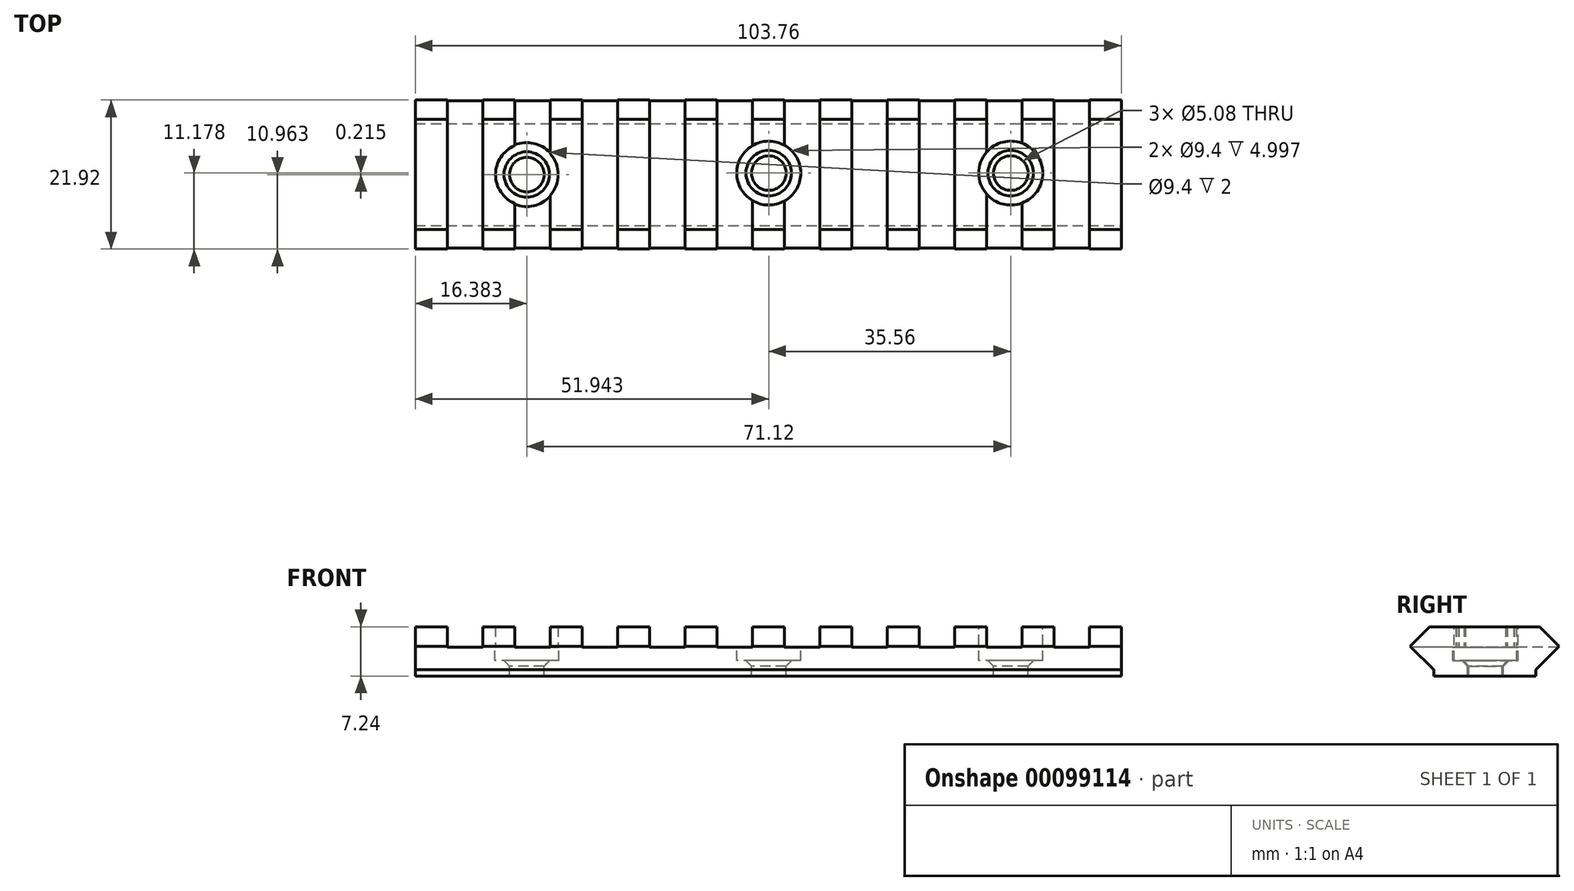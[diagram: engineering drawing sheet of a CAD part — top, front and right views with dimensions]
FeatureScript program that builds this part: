
annotation { "Feature Type Name" : "Feature", "Feature Type Description" : "" }
export const myFeature = defineFeature(function(context is Context, id is Id, definition is map)
    precondition{}
    {
        {
            var Q0;
            Q0=qCreatedBy(makeId("Right.planeOp"),FACE);
            var sketch = newSketch(context, id + "F0", { "sketchPlane" : qUnion([Q0])});
            skLineSegment(sketch, "E0", {"start": v(0, 0) * mm, "end": v(0, 1.52) * mm});
            skLineSegment(sketch, "E1", {"start": v(0, 1.52) * mm, "end": v(-2.86, 4.38) * mm});
            skLineSegment(sketch, "E2", {"start": v(-2.86, 4.38) * mm, "end": v(0, 7.24) * mm});
            skLineSegment(sketch, "E3", {"start": v(0, 7.24) * mm, "end": v(16.2, 7.24) * mm});
            skLineSegment(sketch, "E4", {"start": v(0, 0) * mm, "end": v(16.2, 0) * mm});
            skLineSegment(sketch, "E5", {"start": v(16.2, 0) * mm, "end": v(16.2, 1.52) * mm});
            skLineSegment(sketch, "E6", {"start": v(16.2, 1.52) * mm, "end": v(19.06, 4.38) * mm});
            skLineSegment(sketch, "E7", {"start": v(19.06, 4.38) * mm, "end": v(16.2, 7.24) * mm});
            skSolve(sketch);
        }
        {
            var Q0;
            Q0=makeQuery(id+"F0.imprint","IMPRINT",FACE,{"disambiguationData":[TD([[makeQuery(id+"F0.imprint","IMPRINT",EDGE,{"derivedFrom":sQuery(id+"F0.wireOp",EDGE,"E0")}),-1.0]])]});
            extrude(context, id + "F1", {"entities" : qUnion([Q0]), "depth" : 103.76 * mm});
        }
        {
            var Q0;
            Q0=makeQuery(id+"F1.opExtrude","SWEPT_FACE",FACE,{"disambiguationData":[OSD([sQuery(id+"F0.wireOp",EDGE,"E3")])]});
            var sketch = newSketch(context, id + "F2", { "sketchPlane" : qUnion([Q0])});
            skLineSegment(sketch, "E8", {"start": v(0, 8.1) * mm, "end": v(4.7, 8.1) * mm, "construction": true});
            skLineSegment(sketch, "E9", {"start": v(4.7, 8.1) * mm, "end": v(4.7, 19.06) * mm});
            skLineSegment(sketch, "E10", {"start": v(4.7, 8.1) * mm, "end": v(4.7, -2.86) * mm});
            skLineSegment(sketch, "E11", {"start": v(4.7, 8.1) * mm, "end": v(9.9, 8.1) * mm, "construction": true});
            skLineSegment(sketch, "E12", {"start": v(4.7, 19.06) * mm, "end": v(9.9, 19.06) * mm});
            skLineSegment(sketch, "E13", {"start": v(9.9, 19.06) * mm, "end": v(9.9, -2.86) * mm});
            skLineSegment(sketch, "E14", {"start": v(4.7, -2.86) * mm, "end": v(9.9, -2.86) * mm});
            skLineSegment(sketch, "E15", {"start": v(9.9, 8.1) * mm, "end": v(14.6, 8.1) * mm, "construction": true});
            skLineSegment(sketch, "E16.bottom", {"start": v(14.6, 19.06) * mm, "end": v(19.81, 19.06) * mm});
            skLineSegment(sketch, "E16.top", {"start": v(14.6, -2.86) * mm, "end": v(19.81, -2.86) * mm});
            skLineSegment(sketch, "E16.left", {"start": v(14.6, 19.06) * mm, "end": v(14.6, -2.86) * mm});
            skLineSegment(sketch, "E16.right", {"start": v(19.81, 19.06) * mm, "end": v(19.81, -2.86) * mm});
            skLineSegment(sketch, "E17", {"start": v(19.81, 8.1) * mm, "end": v(24.51, 8.1) * mm, "construction": true});
            skLineSegment(sketch, "E18.bottom", {"start": v(24.51, 19.06) * mm, "end": v(29.72, 19.06) * mm});
            skLineSegment(sketch, "E18.top", {"start": v(24.51, -2.86) * mm, "end": v(29.72, -2.86) * mm});
            skLineSegment(sketch, "E18.left", {"start": v(24.51, 19.06) * mm, "end": v(24.51, -2.86) * mm});
            skLineSegment(sketch, "E18.right", {"start": v(29.72, 19.06) * mm, "end": v(29.72, -2.86) * mm});
            skLineSegment(sketch, "E19.bottom", {"start": v(34.42, 19.06) * mm, "end": v(39.62, 19.06) * mm});
            skLineSegment(sketch, "E19.top", {"start": v(34.42, -2.86) * mm, "end": v(39.62, -2.86) * mm});
            skLineSegment(sketch, "E19.left", {"start": v(34.42, 19.06) * mm, "end": v(34.42, -2.86) * mm});
            skLineSegment(sketch, "E19.right", {"start": v(39.62, 19.06) * mm, "end": v(39.62, -2.86) * mm});
            skLineSegment(sketch, "E20", {"start": v(39.62, 8.1) * mm, "end": v(44.32, 8.1) * mm, "construction": true});
            skLineSegment(sketch, "E21.bottom", {"start": v(44.32, 19.06) * mm, "end": v(49.53, 19.06) * mm});
            skLineSegment(sketch, "E21.top", {"start": v(44.32, -2.86) * mm, "end": v(49.53, -2.86) * mm});
            skLineSegment(sketch, "E21.left", {"start": v(44.32, 19.06) * mm, "end": v(44.32, -2.86) * mm});
            skLineSegment(sketch, "E21.right", {"start": v(49.53, 19.06) * mm, "end": v(49.53, -2.86) * mm});
            skLineSegment(sketch, "E22", {"start": v(49.53, 8.1) * mm, "end": v(54.23, 8.1) * mm, "construction": true});
            skLineSegment(sketch, "E23.bottom", {"start": v(54.23, 19.06) * mm, "end": v(59.44, 19.06) * mm});
            skLineSegment(sketch, "E23.top", {"start": v(54.23, -2.86) * mm, "end": v(59.44, -2.86) * mm});
            skLineSegment(sketch, "E23.left", {"start": v(54.23, 19.06) * mm, "end": v(54.23, -2.86) * mm});
            skLineSegment(sketch, "E23.right", {"start": v(59.44, 19.06) * mm, "end": v(59.44, -2.86) * mm});
            skLineSegment(sketch, "E24", {"start": v(59.44, 8.1) * mm, "end": v(64.13, 8.1) * mm, "construction": true});
            skLineSegment(sketch, "E25.bottom", {"start": v(64.13, 19.06) * mm, "end": v(69.34, 19.06) * mm});
            skLineSegment(sketch, "E25.top", {"start": v(64.13, -2.86) * mm, "end": v(69.34, -2.86) * mm});
            skLineSegment(sketch, "E25.left", {"start": v(64.13, 19.06) * mm, "end": v(64.13, -2.86) * mm});
            skLineSegment(sketch, "E25.right", {"start": v(69.34, 19.06) * mm, "end": v(69.34, -2.86) * mm});
            skLineSegment(sketch, "E26", {"start": v(69.34, 8.1) * mm, "end": v(74.04, 8.1) * mm, "construction": true});
            skLineSegment(sketch, "E27", {"start": v(29.72, 8.1) * mm, "end": v(34.42, 8.1) * mm, "construction": true});
            skLineSegment(sketch, "E28.bottom", {"start": v(74.04, 19.06) * mm, "end": v(79.25, 19.06) * mm});
            skLineSegment(sketch, "E28.top", {"start": v(74.04, -2.86) * mm, "end": v(79.25, -2.86) * mm});
            skLineSegment(sketch, "E28.left", {"start": v(74.04, 19.06) * mm, "end": v(74.04, -2.86) * mm});
            skLineSegment(sketch, "E28.right", {"start": v(79.25, 19.06) * mm, "end": v(79.25, -2.86) * mm});
            skLineSegment(sketch, "E29", {"start": v(79.25, 8.1) * mm, "end": v(83.95, 8.1) * mm, "construction": true});
            skLineSegment(sketch, "E30.bottom", {"start": v(83.95, 19.06) * mm, "end": v(89.15, 19.06) * mm});
            skLineSegment(sketch, "E30.top", {"start": v(83.95, -2.86) * mm, "end": v(89.15, -2.86) * mm});
            skLineSegment(sketch, "E30.left", {"start": v(83.95, 19.06) * mm, "end": v(83.95, -2.86) * mm});
            skLineSegment(sketch, "E30.right", {"start": v(89.15, 19.06) * mm, "end": v(89.15, -2.86) * mm});
            skLineSegment(sketch, "E31", {"start": v(89.15, 8.1) * mm, "end": v(93.85, 8.1) * mm, "construction": true});
            skLineSegment(sketch, "E32.bottom", {"start": v(93.85, 19.15) * mm, "end": v(99.06, 19.15) * mm});
            skLineSegment(sketch, "E32.top", {"start": v(93.85, -2.94) * mm, "end": v(99.06, -2.94) * mm});
            skLineSegment(sketch, "E32.left", {"start": v(93.85, 19.15) * mm, "end": v(93.85, -2.94) * mm});
            skLineSegment(sketch, "E32.right", {"start": v(99.06, 19.15) * mm, "end": v(99.06, -2.94) * mm});
            skSolve(sketch);
        }
        {
            var Q0;
            {var subQ0=sQuery(id+"F2.wireOp",EDGE,"E14");Q0=makeQuery(id+"F2.imprint","IMPRINT",FACE,{"disambiguationData":[TD([[makeQuery(id+"F2.imprint","IMPRINT",EDGE,{"derivedFrom":subQ0}),1.0]])]});}
            var Q1;
            {var subQ0=sQuery(id+"F2.wireOp",EDGE,"E10");var subQ8=sQuery(id+"F2.wireOp",EDGE,"E9");var subQ9=makeQuery(id+"F2.imprint","INTERSECT",VERTEX,{"derivedFrom":[subQ8,subQ0]});Q1=makeQuery(id+"F2.imprint","IMPRINT",FACE,{"disambiguationData":[TD([[makeQuery(id+"F2.imprint","IMPRINT",EDGE,{"disambiguationData":[TD([[subQ9,-1.0]])],"derivedFrom":subQ8}),-1.0]])]});}
            var Q2;
            {var subQ0=sQuery(id+"F2.wireOp",EDGE,"E12");Q2=makeQuery(id+"F2.imprint","IMPRINT",FACE,{"disambiguationData":[TD([[makeQuery(id+"F2.imprint","IMPRINT",EDGE,{"derivedFrom":subQ0}),-1.0]])]});}
            var Q3;
            {var subQ0=sQuery(id+"F2.wireOp",EDGE,"E16.bottom");Q3=makeQuery(id+"F2.imprint","IMPRINT",FACE,{"disambiguationData":[TD([[makeQuery(id+"F2.imprint","IMPRINT",EDGE,{"derivedFrom":subQ0}),-1.0]])]});}
            var Q4;
            {var subQ0=sQuery(id+"F2.wireOp",EDGE,"E16.left");var subQ1=sQuery(id+"F0.wireOp",EDGE,"E3");var subQ2=makeQuery(id+"F1.opExtrude","SWEPT_EDGE",EDGE,{"disambiguationData":[OSD([subQ1,sQuery(id+"F0.wireOp",EDGE,"E7")])]});var subQ3=makeQuery(id+"F2.imprint","INTERSECT",VERTEX,{"derivedFrom":[subQ2,subQ0]});Q4=makeQuery(id+"F2.imprint","IMPRINT",FACE,{"disambiguationData":[TD([[makeQuery(id+"F2.imprint","IMPRINT",EDGE,{"disambiguationData":[TD([[subQ3,-1.0]])],"derivedFrom":subQ0}),1.0]])]});}
            var Q5;
            {var subQ0=sQuery(id+"F2.wireOp",EDGE,"E16.top");Q5=makeQuery(id+"F2.imprint","IMPRINT",FACE,{"disambiguationData":[TD([[makeQuery(id+"F2.imprint","IMPRINT",EDGE,{"derivedFrom":subQ0}),1.0]])]});}
            var Q6;
            {var subQ0=sQuery(id+"F2.wireOp",EDGE,"E18.bottom");Q6=makeQuery(id+"F2.imprint","IMPRINT",FACE,{"disambiguationData":[TD([[makeQuery(id+"F2.imprint","IMPRINT",EDGE,{"derivedFrom":subQ0}),-1.0]])]});}
            var Q7;
            {var subQ0=sQuery(id+"F2.wireOp",EDGE,"E18.left");var subQ1=sQuery(id+"F0.wireOp",EDGE,"E3");var subQ2=makeQuery(id+"F1.opExtrude","SWEPT_EDGE",EDGE,{"disambiguationData":[OSD([subQ1,sQuery(id+"F0.wireOp",EDGE,"E7")])]});var subQ3=makeQuery(id+"F2.imprint","INTERSECT",VERTEX,{"derivedFrom":[subQ2,subQ0]});Q7=makeQuery(id+"F2.imprint","IMPRINT",FACE,{"disambiguationData":[TD([[makeQuery(id+"F2.imprint","IMPRINT",EDGE,{"disambiguationData":[TD([[subQ3,-1.0]])],"derivedFrom":subQ0}),1.0]])]});}
            var Q8;
            {var subQ0=sQuery(id+"F2.wireOp",EDGE,"E18.top");Q8=makeQuery(id+"F2.imprint","IMPRINT",FACE,{"disambiguationData":[TD([[makeQuery(id+"F2.imprint","IMPRINT",EDGE,{"derivedFrom":subQ0}),1.0]])]});}
            var Q9;
            {var subQ0=sQuery(id+"F2.wireOp",EDGE,"E19.bottom");Q9=makeQuery(id+"F2.imprint","IMPRINT",FACE,{"disambiguationData":[TD([[makeQuery(id+"F2.imprint","IMPRINT",EDGE,{"derivedFrom":subQ0}),-1.0]])]});}
            var Q10;
            {var subQ0=sQuery(id+"F2.wireOp",EDGE,"E19.left");var subQ1=sQuery(id+"F0.wireOp",EDGE,"E3");var subQ2=makeQuery(id+"F1.opExtrude","SWEPT_EDGE",EDGE,{"disambiguationData":[OSD([subQ1,sQuery(id+"F0.wireOp",EDGE,"E7")])]});var subQ3=makeQuery(id+"F2.imprint","INTERSECT",VERTEX,{"derivedFrom":[subQ2,subQ0]});Q10=makeQuery(id+"F2.imprint","IMPRINT",FACE,{"disambiguationData":[TD([[makeQuery(id+"F2.imprint","IMPRINT",EDGE,{"disambiguationData":[TD([[subQ3,-1.0]])],"derivedFrom":subQ0}),1.0]])]});}
            var Q11;
            {var subQ0=sQuery(id+"F2.wireOp",EDGE,"E19.top");Q11=makeQuery(id+"F2.imprint","IMPRINT",FACE,{"disambiguationData":[TD([[makeQuery(id+"F2.imprint","IMPRINT",EDGE,{"derivedFrom":subQ0}),1.0]])]});}
            var Q12;
            {var subQ0=sQuery(id+"F2.wireOp",EDGE,"E21.bottom");Q12=makeQuery(id+"F2.imprint","IMPRINT",FACE,{"disambiguationData":[TD([[makeQuery(id+"F2.imprint","IMPRINT",EDGE,{"derivedFrom":subQ0}),-1.0]])]});}
            var Q13;
            {var subQ0=sQuery(id+"F2.wireOp",EDGE,"E21.left");var subQ1=sQuery(id+"F0.wireOp",EDGE,"E3");var subQ2=makeQuery(id+"F1.opExtrude","SWEPT_EDGE",EDGE,{"disambiguationData":[OSD([subQ1,sQuery(id+"F0.wireOp",EDGE,"E7")])]});var subQ3=makeQuery(id+"F2.imprint","INTERSECT",VERTEX,{"derivedFrom":[subQ2,subQ0]});Q13=makeQuery(id+"F2.imprint","IMPRINT",FACE,{"disambiguationData":[TD([[makeQuery(id+"F2.imprint","IMPRINT",EDGE,{"disambiguationData":[TD([[subQ3,-1.0]])],"derivedFrom":subQ0}),1.0]])]});}
            var Q14;
            {var subQ0=sQuery(id+"F2.wireOp",EDGE,"E21.top");Q14=makeQuery(id+"F2.imprint","IMPRINT",FACE,{"disambiguationData":[TD([[makeQuery(id+"F2.imprint","IMPRINT",EDGE,{"derivedFrom":subQ0}),1.0]])]});}
            var Q15;
            {var subQ0=sQuery(id+"F2.wireOp",EDGE,"E23.bottom");Q15=makeQuery(id+"F2.imprint","IMPRINT",FACE,{"disambiguationData":[TD([[makeQuery(id+"F2.imprint","IMPRINT",EDGE,{"derivedFrom":subQ0}),-1.0]])]});}
            var Q16;
            {var subQ0=sQuery(id+"F2.wireOp",EDGE,"E23.left");var subQ1=sQuery(id+"F0.wireOp",EDGE,"E3");var subQ2=makeQuery(id+"F1.opExtrude","SWEPT_EDGE",EDGE,{"disambiguationData":[OSD([subQ1,sQuery(id+"F0.wireOp",EDGE,"E7")])]});var subQ3=makeQuery(id+"F2.imprint","INTERSECT",VERTEX,{"derivedFrom":[subQ2,subQ0]});Q16=makeQuery(id+"F2.imprint","IMPRINT",FACE,{"disambiguationData":[TD([[makeQuery(id+"F2.imprint","IMPRINT",EDGE,{"disambiguationData":[TD([[subQ3,-1.0]])],"derivedFrom":subQ0}),1.0]])]});}
            var Q17;
            {var subQ0=sQuery(id+"F2.wireOp",EDGE,"E23.top");Q17=makeQuery(id+"F2.imprint","IMPRINT",FACE,{"disambiguationData":[TD([[makeQuery(id+"F2.imprint","IMPRINT",EDGE,{"derivedFrom":subQ0}),1.0]])]});}
            var Q18;
            {var subQ0=sQuery(id+"F2.wireOp",EDGE,"E25.bottom");Q18=makeQuery(id+"F2.imprint","IMPRINT",FACE,{"disambiguationData":[TD([[makeQuery(id+"F2.imprint","IMPRINT",EDGE,{"derivedFrom":subQ0}),-1.0]])]});}
            var Q19;
            {var subQ0=sQuery(id+"F2.wireOp",EDGE,"E25.left");var subQ1=sQuery(id+"F0.wireOp",EDGE,"E3");var subQ2=makeQuery(id+"F1.opExtrude","SWEPT_EDGE",EDGE,{"disambiguationData":[OSD([subQ1,sQuery(id+"F0.wireOp",EDGE,"E7")])]});var subQ3=makeQuery(id+"F2.imprint","INTERSECT",VERTEX,{"derivedFrom":[subQ2,subQ0]});Q19=makeQuery(id+"F2.imprint","IMPRINT",FACE,{"disambiguationData":[TD([[makeQuery(id+"F2.imprint","IMPRINT",EDGE,{"disambiguationData":[TD([[subQ3,-1.0]])],"derivedFrom":subQ0}),1.0]])]});}
            var Q20;
            {var subQ0=sQuery(id+"F2.wireOp",EDGE,"E25.top");Q20=makeQuery(id+"F2.imprint","IMPRINT",FACE,{"disambiguationData":[TD([[makeQuery(id+"F2.imprint","IMPRINT",EDGE,{"derivedFrom":subQ0}),1.0]])]});}
            var Q21;
            {var subQ0=sQuery(id+"F2.wireOp",EDGE,"E28.bottom");Q21=makeQuery(id+"F2.imprint","IMPRINT",FACE,{"disambiguationData":[TD([[makeQuery(id+"F2.imprint","IMPRINT",EDGE,{"derivedFrom":subQ0}),-1.0]])]});}
            var Q22;
            {var subQ0=sQuery(id+"F2.wireOp",EDGE,"E28.left");var subQ1=sQuery(id+"F0.wireOp",EDGE,"E3");var subQ2=makeQuery(id+"F1.opExtrude","SWEPT_EDGE",EDGE,{"disambiguationData":[OSD([subQ1,sQuery(id+"F0.wireOp",EDGE,"E7")])]});var subQ3=makeQuery(id+"F2.imprint","INTERSECT",VERTEX,{"derivedFrom":[subQ2,subQ0]});Q22=makeQuery(id+"F2.imprint","IMPRINT",FACE,{"disambiguationData":[TD([[makeQuery(id+"F2.imprint","IMPRINT",EDGE,{"disambiguationData":[TD([[subQ3,-1.0]])],"derivedFrom":subQ0}),1.0]])]});}
            var Q23;
            {var subQ0=sQuery(id+"F2.wireOp",EDGE,"E28.top");Q23=makeQuery(id+"F2.imprint","IMPRINT",FACE,{"disambiguationData":[TD([[makeQuery(id+"F2.imprint","IMPRINT",EDGE,{"derivedFrom":subQ0}),1.0]])]});}
            var Q24;
            {var subQ0=sQuery(id+"F2.wireOp",EDGE,"E30.top");Q24=makeQuery(id+"F2.imprint","IMPRINT",FACE,{"disambiguationData":[TD([[makeQuery(id+"F2.imprint","IMPRINT",EDGE,{"derivedFrom":subQ0}),1.0]])]});}
            var Q25;
            {var subQ0=sQuery(id+"F2.wireOp",EDGE,"E30.left");var subQ1=sQuery(id+"F0.wireOp",EDGE,"E3");var subQ2=makeQuery(id+"F1.opExtrude","SWEPT_EDGE",EDGE,{"disambiguationData":[OSD([subQ1,sQuery(id+"F0.wireOp",EDGE,"E7")])]});var subQ3=makeQuery(id+"F2.imprint","INTERSECT",VERTEX,{"derivedFrom":[subQ2,subQ0]});Q25=makeQuery(id+"F2.imprint","IMPRINT",FACE,{"disambiguationData":[TD([[makeQuery(id+"F2.imprint","IMPRINT",EDGE,{"disambiguationData":[TD([[subQ3,-1.0]])],"derivedFrom":subQ0}),1.0]])]});}
            var Q26;
            {var subQ0=sQuery(id+"F2.wireOp",EDGE,"E30.bottom");Q26=makeQuery(id+"F2.imprint","IMPRINT",FACE,{"disambiguationData":[TD([[makeQuery(id+"F2.imprint","IMPRINT",EDGE,{"derivedFrom":subQ0}),-1.0]])]});}
            var Q27;
            {var subQ0=sQuery(id+"F2.wireOp",EDGE,"E32.bottom");Q27=makeQuery(id+"F2.imprint","IMPRINT",FACE,{"disambiguationData":[TD([[makeQuery(id+"F2.imprint","IMPRINT",EDGE,{"derivedFrom":subQ0}),-1.0]])]});}
            var Q28;
            {var subQ0=sQuery(id+"F2.wireOp",EDGE,"E32.left");var subQ1=sQuery(id+"F0.wireOp",EDGE,"E3");var subQ2=makeQuery(id+"F1.opExtrude","SWEPT_EDGE",EDGE,{"disambiguationData":[OSD([subQ1,sQuery(id+"F0.wireOp",EDGE,"E7")])]});var subQ3=makeQuery(id+"F2.imprint","INTERSECT",VERTEX,{"derivedFrom":[subQ2,subQ0]});Q28=makeQuery(id+"F2.imprint","IMPRINT",FACE,{"disambiguationData":[TD([[makeQuery(id+"F2.imprint","IMPRINT",EDGE,{"disambiguationData":[TD([[subQ3,-1.0]])],"derivedFrom":subQ0}),1.0]])]});}
            var Q29;
            {var subQ0=sQuery(id+"F2.wireOp",EDGE,"E32.top");Q29=makeQuery(id+"F2.imprint","IMPRINT",FACE,{"disambiguationData":[TD([[makeQuery(id+"F2.imprint","IMPRINT",EDGE,{"derivedFrom":subQ0}),1.0]])]});}
            extrude(context, id + "F3", {"entities" : qUnion([Q0, Q1, Q2, Q3, Q4, Q5, Q6, Q7, Q8, Q9, Q10, Q11, Q12, Q13, Q14, Q15, Q16, Q17, Q18, Q19, Q20, Q21, Q22, Q23, Q24, Q25, Q26, Q27, Q28, Q29]), "operationType" : NewBodyOperationType.REMOVE, "oppositeDirection" : true, "depth" : 3 * mm});
        }
        {
            var Q0;
            Q0=makeQuery(id+"F1.opExtrude","SWEPT_FACE",FACE,{"disambiguationData":[OSD([sQuery(id+"F0.wireOp",EDGE,"E4")])]});
            var sketch = newSketch(context, id + "F4", { "sketchPlane" : qUnion([Q0])});
            skCircle(sketch, "E33", {"center": v(87.5, -8.32) * mm, "radius": 2.54 * mm});
            skCircle(sketch, "E34", {"center": v(16.38, -8.1) * mm, "radius": 2.54 * mm});
            skLineSegment(sketch, "E35", {"start": v(16.38, -8.1) * mm, "end": v(0, -8.1) * mm, "construction": true});
            skPoint(sketch, "E35.endSnap0", {"position": v(0, -8.1) * mm});
            skCircle(sketch, "E36", {"center": v(51.94, -8.32) * mm, "radius": 2.54 * mm});
            skSolve(sketch);
        }
        {
            var Q0;
            Q0 = qSketchRegion(id + "F4", true);
            extrude(context, id + "F5", {"entities" : qUnion([Q0]), "operationType" : NewBodyOperationType.REMOVE, "endBound" : BoundingType.SYMMETRIC, "depth" : 25.4 * mm, "offsetDistance" : 25.4 * mm});
        }
        {
            var Q0;
            Q0=makeQuery(id+"F3.boolean.opBoolean","COPY",FACE,{"derivedFrom":makeQuery(id+"F3.opExtrude","CAP_FACE",FACE,{"disambiguationData":[OSD([sQuery(id+"F2.wireOp",EDGE,"E16.bottom"),sQuery(id+"F2.wireOp",EDGE,"E16.top"),sQuery(id+"F2.wireOp",EDGE,"E16.left"),sQuery(id+"F2.wireOp",EDGE,"E16.right")])],"isStart":false})});
            var sketch = newSketch(context, id + "F6", { "sketchPlane" : qUnion([Q0])});
            skCircle(sketch, "E37", {"center": v(16.38, 8.1) * mm, "radius": 4.6 * mm});
            skSolve(sketch);
        }
        {
            var Q0;
            Q0 = qSketchRegion(id + "F6", true);
            extrude(context, id + "F7", {"entities" : qUnion([Q0]), "operationType" : NewBodyOperationType.REMOVE, "depth" : 25.4 * mm, "offsetDistance" : 25.4 * mm});
        }
        {
            var Q0;
            Q0=makeQuery(id+"F3.boolean.opBoolean","COPY",FACE,{"derivedFrom":makeQuery(id+"F3.opExtrude","CAP_FACE",FACE,{"disambiguationData":[OSD([sQuery(id+"F2.wireOp",EDGE,"E30.bottom"),sQuery(id+"F2.wireOp",EDGE,"E30.top"),sQuery(id+"F2.wireOp",EDGE,"E30.left"),sQuery(id+"F2.wireOp",EDGE,"E30.right")])],"isStart":false})});
            var sketch = newSketch(context, id + "F8", { "sketchPlane" : qUnion([Q0])});
            skCircle(sketch, "E38", {"center": v(87.5, 8.32) * mm, "radius": 4.6 * mm});
            skSolve(sketch);
        }
        {
            var Q0;
            Q0 = qSketchRegion(id + "F8", true);
            extrude(context, id + "F9", {"entities" : qUnion([Q0]), "operationType" : NewBodyOperationType.REMOVE, "depth" : 25.4 * mm, "offsetDistance" : 25.4 * mm});
        }
        {
            var Q0;
            Q0=makeQuery(id+"F3.boolean.opBoolean","COPY",FACE,{"derivedFrom":makeQuery(id+"F3.opExtrude","CAP_FACE",FACE,{"disambiguationData":[OSD([sQuery(id+"F2.wireOp",EDGE,"E23.bottom"),sQuery(id+"F2.wireOp",EDGE,"E23.top"),sQuery(id+"F2.wireOp",EDGE,"E23.left"),sQuery(id+"F2.wireOp",EDGE,"E23.right")])],"isStart":false})});
            var sketch = newSketch(context, id + "F10", { "sketchPlane" : qUnion([Q0])});
            skCircle(sketch, "E39", {"center": v(51.94, 8.32) * mm, "radius": 4.6 * mm});
            skSolve(sketch);
        }
        {
            var Q0;
            Q0 = qSketchRegion(id + "F10", true);
            extrude(context, id + "F11", {"entities" : qUnion([Q0]), "operationType" : NewBodyOperationType.REMOVE, "depth" : 25.4 * mm, "offsetDistance" : 25.4 * mm});
        }
        {
            var Q0;
            Q0=makeQuery(id+"F1.opExtrude","CAP_FACE",FACE,{"disambiguationData":[OSD([sQuery(id+"F0.wireOp",EDGE,"E0"),sQuery(id+"F0.wireOp",EDGE,"E1"),sQuery(id+"F0.wireOp",EDGE,"E2"),sQuery(id+"F0.wireOp",EDGE,"E3"),sQuery(id+"F0.wireOp",EDGE,"E4"),sQuery(id+"F0.wireOp",EDGE,"E5"),sQuery(id+"F0.wireOp",EDGE,"E6"),sQuery(id+"F0.wireOp",EDGE,"E7")])],"isStart":false});
            var sketch = newSketch(context, id + "F12", { "sketchPlane" : qUnion([Q0])});
            skLineSegment(sketch, "E40", {"start": v(-2.86, 4.38) * mm, "end": v(0.6, 0.92) * mm});
            skLineSegment(sketch, "E41", {"start": v(19.06, 4.38) * mm, "end": v(15.6, 0.92) * mm});
            skLineSegment(sketch, "E42", {"start": v(0.6, 0) * mm, "end": v(0.6, 0.92) * mm});
            skLineSegment(sketch, "E43", {"start": v(-2.86, 4.38) * mm, "end": v(-2.86, 0) * mm});
            skLineSegment(sketch, "E44", {"start": v(-2.86, 0) * mm, "end": v(0.6, 0) * mm});
            skLineSegment(sketch, "E45", {"start": v(15.6, 0.92) * mm, "end": v(15.6, 0) * mm});
            skLineSegment(sketch, "E46", {"start": v(15.6, 0) * mm, "end": v(19.06, 0) * mm});
            skLineSegment(sketch, "E47", {"start": v(19.06, 0) * mm, "end": v(19.06, 4.38) * mm});
            skSolve(sketch);
        }
        {
            var Q0;
            Q0 = qSketchRegion(id + "F12", true);
            extrude(context, id + "F13", {"entities" : qUnion([Q0]), "operationType" : NewBodyOperationType.REMOVE, "oppositeDirection" : true, "depth" : 127 * mm, "offsetDistance" : 25.4 * mm});
        }
        {
            var Q0;
            Q0=makeQuery(id+"F7.boolean.opBoolean","MERGE",FACE,{"derivedFrom":[makeQuery(id+"F3.boolean.opBoolean","COPY",FACE,{"derivedFrom":makeQuery(id+"F3.opExtrude","CAP_FACE",FACE,{"disambiguationData":[OSD([sQuery(id+"F2.wireOp",EDGE,"E16.bottom"),sQuery(id+"F2.wireOp",EDGE,"E16.top"),sQuery(id+"F2.wireOp",EDGE,"E16.left"),sQuery(id+"F2.wireOp",EDGE,"E16.right")])],"isStart":false})})],"fromTools":[makeQuery(id+"F7.opExtrude","CAP_FACE",FACE,{"disambiguationData":[OSD([sQuery(id+"F6.wireOp",EDGE,"E37")])],"isStart":true})]});
            var sketch = newSketch(context, id + "F14", { "sketchPlane" : qUnion([Q0])});
            skCircle(sketch, "E48", {"center": v(16.38, 8.1) * mm, "radius": 4.7 * mm});
            skSolve(sketch);
        }
        {
            var Q0;
            Q0 = qSketchRegion(id + "F14", true);
            extrude(context, id + "F15", {"entities" : qUnion([Q0]), "operationType" : NewBodyOperationType.REMOVE, "oppositeDirection" : true, "depth" : 2 * mm, "offsetDistance" : 25.4 * mm});
        }
        {
            var Q0;
            Q0=makeQuery(id+"F11.boolean.opBoolean","MERGE",FACE,{"derivedFrom":[makeQuery(id+"F3.boolean.opBoolean","COPY",FACE,{"derivedFrom":makeQuery(id+"F3.opExtrude","CAP_FACE",FACE,{"disambiguationData":[OSD([sQuery(id+"F2.wireOp",EDGE,"E21.bottom"),sQuery(id+"F2.wireOp",EDGE,"E21.top"),sQuery(id+"F2.wireOp",EDGE,"E21.left"),sQuery(id+"F2.wireOp",EDGE,"E21.right")])],"isStart":false})}),makeQuery(id+"F3.boolean.opBoolean","COPY",FACE,{"derivedFrom":makeQuery(id+"F3.opExtrude","CAP_FACE",FACE,{"disambiguationData":[OSD([sQuery(id+"F2.wireOp",EDGE,"E23.bottom"),sQuery(id+"F2.wireOp",EDGE,"E23.top"),sQuery(id+"F2.wireOp",EDGE,"E23.left"),sQuery(id+"F2.wireOp",EDGE,"E23.right")])],"isStart":false})})],"fromTools":[makeQuery(id+"F11.opExtrude","CAP_FACE",FACE,{"disambiguationData":[OSD([sQuery(id+"F10.wireOp",EDGE,"E39")])],"isStart":true})]});
            var sketch = newSketch(context, id + "F16", { "sketchPlane" : qUnion([Q0])});
            skCircle(sketch, "E49", {"center": v(51.94, 8.32) * mm, "radius": 4.7 * mm});
            skSolve(sketch);
        }
        {
            var Q0;
            Q0 = qSketchRegion(id + "F16", true);
            extrude(context, id + "F17", {"entities" : qUnion([Q0]), "operationType" : NewBodyOperationType.REMOVE, "oppositeDirection" : true, "depth" : 2 * mm, "offsetDistance" : 25.4 * mm});
        }
        {
            var Q0;
            Q0 = qSketchRegion(id + "F16", true);
            extrude(context, id + "F18", {"entities" : qUnion([Q0]), "operationType" : NewBodyOperationType.REMOVE, "depth" : 25.4 * mm, "offsetDistance" : 25.4 * mm});
        }
        {
            var Q0;
            Q0=makeQuery(id+"F9.boolean.opBoolean","MERGE",FACE,{"derivedFrom":[makeQuery(id+"F3.boolean.opBoolean","COPY",FACE,{"derivedFrom":makeQuery(id+"F3.opExtrude","CAP_FACE",FACE,{"disambiguationData":[OSD([sQuery(id+"F2.wireOp",EDGE,"E30.bottom"),sQuery(id+"F2.wireOp",EDGE,"E30.top"),sQuery(id+"F2.wireOp",EDGE,"E30.left"),sQuery(id+"F2.wireOp",EDGE,"E30.right")])],"isStart":false})})],"fromTools":[makeQuery(id+"F9.opExtrude","CAP_FACE",FACE,{"disambiguationData":[OSD([sQuery(id+"F8.wireOp",EDGE,"E38")])],"isStart":true})]});
            var sketch = newSketch(context, id + "F19", { "sketchPlane" : qUnion([Q0])});
            skCircle(sketch, "E50", {"center": v(87.5, 8.32) * mm, "radius": 4.7 * mm});
            skSolve(sketch);
        }
        {
            var Q0;
            Q0 = qSketchRegion(id + "F19", true);
            extrude(context, id + "F20", {"entities" : qUnion([Q0]), "operationType" : NewBodyOperationType.REMOVE, "oppositeDirection" : true, "depth" : 2 * mm, "offsetDistance" : 25.4 * mm});
        }
        {
            var Q0;
            Q0 = qSketchRegion(id + "F19", true);
            extrude(context, id + "F21", {"entities" : qUnion([Q0]), "operationType" : NewBodyOperationType.REMOVE, "depth" : 25.4 * mm, "offsetDistance" : 25.4 * mm});
        }
        {
            var Q0;
            Q0=makeQuery(id+"F20.boolean.opBoolean","INTERSECT",EDGE,{"derivedFrom":[makeQuery(id+"F5.boolean.opBoolean","COPY",FACE,{"derivedFrom":makeQuery(id+"F5.opExtrude","SWEPT_FACE",FACE,{"disambiguationData":[OSD([sQuery(id+"F4.wireOp",EDGE,"E33")])]})}),makeQuery(id+"F20.opExtrude","CAP_FACE",FACE,{"disambiguationData":[OSD([sQuery(id+"F19.wireOp",EDGE,"E50")])],"isStart":false})]});
            var Q1;
            Q1=makeQuery(id+"F17.boolean.opBoolean","INTERSECT",EDGE,{"derivedFrom":[makeQuery(id+"F5.boolean.opBoolean","COPY",FACE,{"derivedFrom":makeQuery(id+"F5.opExtrude","SWEPT_FACE",FACE,{"disambiguationData":[OSD([sQuery(id+"F4.wireOp",EDGE,"E36")])]})}),makeQuery(id+"F17.opExtrude","CAP_FACE",FACE,{"disambiguationData":[OSD([sQuery(id+"F16.wireOp",EDGE,"E49")])],"isStart":false})]});
            var Q2;
            Q2=makeQuery(id+"F15.boolean.opBoolean","INTERSECT",EDGE,{"derivedFrom":[makeQuery(id+"F5.boolean.opBoolean","COPY",FACE,{"derivedFrom":makeQuery(id+"F5.opExtrude","SWEPT_FACE",FACE,{"disambiguationData":[OSD([sQuery(id+"F4.wireOp",EDGE,"E34")])]})}),makeQuery(id+"F15.opExtrude","CAP_FACE",FACE,{"disambiguationData":[OSD([sQuery(id+"F14.wireOp",EDGE,"E48")])],"isStart":false})]});
            chamfer(context, id + "F22", {"entities" : qUnion([Q0, Q1, Q2]), "width" : 0.8 * mm, "tangentPropagation" : true});
        }
    });
